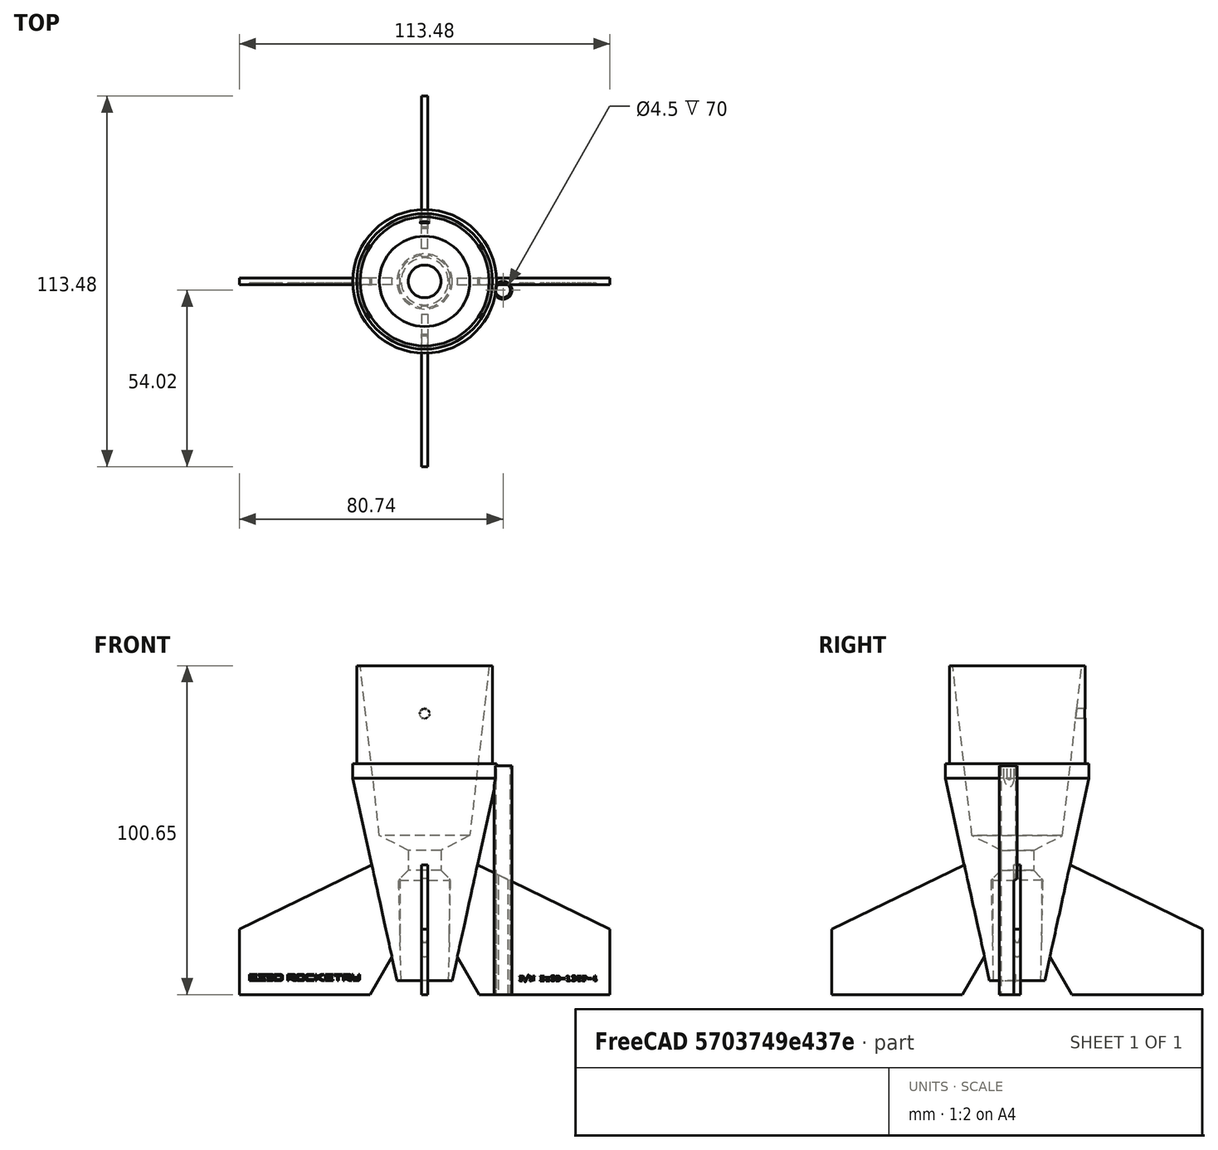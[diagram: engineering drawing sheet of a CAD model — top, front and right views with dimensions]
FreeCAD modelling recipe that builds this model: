
FCSTD DOCUMENT  (FreeCAD 0.20R29603 (Git))
Label: Ez3D-13TP-4
License: All rights reserved
LicenseURL: http://en.wikipedia.org/wiki/All_rights_reserved
objects: Sketcher::SketchObject×4, PartDesign::Pad×2, Part::Part2DObjectPython×2, PartDesign::Pocket×2, PartDesign::Revolution×1, PartDesign::PolarPattern×1, Mesh::Feature×1, PartDesign::Plane×1, PartDesign::Hole×1, PartDesign::Body×1
note: 21 computed .brp shape members not serialized (recipe doc carries the construction recipe); baked Part::Feature solids carry a one-line shape summary decoded from their .brp

FEATURE [Sketcher::SketchObject] Sketch  label="Fin Can and Transition"
  FullyConstrained = false
  MapMode = 5
  Placement = pos=(0,0,0) rot=(1,0,0;1.5708rad)
  Support = -> [XZ_Plane]
  sketch-geometry (11):
    g0: LineSegment StartX=5 StartY=44.1548 StartZ=0 EndX=5 EndY=38 EndZ=0
    g1: LineSegment StartX=5 StartY=38 StartZ=0 EndX=8 EndY=35 EndZ=0
    g2: LineSegment StartX=8 StartY=35 StartZ=0 EndX=7.21115 EndY=4.32256 EndZ=0
    g3: LineSegment StartX=8.47333 StartY=4.32256 StartZ=0 EndX=22 EndY=66.1942 EndZ=0
    g4: LineSegment StartX=19.75 StartY=100.646 StartZ=0 EndX=13.84 EndY=48.6709 EndZ=0
    g5: LineSegment StartX=13.84 StartY=48.6709 StartZ=0 EndX=5 EndY=44.1548 EndZ=0
    g6: LineSegment StartX=20.75 StartY=70.646 StartZ=0 EndX=20.75 EndY=100.646 EndZ=0
    g7: LineSegment StartX=20.75 StartY=100.646 StartZ=0 EndX=19.75 EndY=100.646 EndZ=0
    g8: LineSegment StartX=20.75 StartY=70.646 StartZ=0 EndX=22 EndY=70.646 EndZ=0
    g9: LineSegment StartX=22 StartY=66.1942 StartZ=0 EndX=22 EndY=70.646 EndZ=0
    g10: LineSegment StartX=8.47333 StartY=4.32256 StartZ=0 EndX=7.21115 EndY=4.32256 EndZ=0
  constraints (25):
    c: Vertical(g0)
    c: Coincident(g0,g1)
    c: Coincident(g1,g2)
    c: Angle(g1) = -0.785398
    c: DistanceX(g-1,g0) = 5
    c: Coincident(g4,g5)
    c: Coincident(g0,g5)
    c: Coincident(g6,g7)
    c: Coincident(g7,g4)
    c: Horizontal(g7)
    c: DistanceX(g-1,g6) = 20.75
    c: DistanceX(g7,g7) = 1
    c: DistanceX(g-1,g3) = 22
    c: Horizontal(g8)
    c: Coincident(g6,g8)
    c: DistanceY(g6,g6) = 30
    c: DistanceX(g-1,g1) = 8
    c: Vertical(g6)
    c: Coincident(g9,g3)
    c: Coincident(g9,g8)
    c: Vertical(g9)
    c: Coincident(g10,g3)
    c: Horizontal(g10)
    c: Coincident(g2,g10)
    c: DistanceY(g-1,g6) = 70.646
FEATURE [PartDesign::Revolution] Revolution  label="Revolution for Fin Can"
  Angle = 360
  Axis = (0,-2e-16,1)
  Base = (0,0,0)
  Placement = pos=(0,0,0) rot=(1,0,0;1.5708rad)
  Profile = -> Sketch
  ReferenceAxis = -> Sketch [V_Axis]
  Reversed = true
FEATURE [Sketcher::SketchObject] Sketch001  label="Fin"
  FullyConstrained = true
  MapMode = 5
  Placement = pos=(0,0,0) rot=(1,0,0;1.5708rad)
  Support = -> [XZ_Plane]
  sketch-geometry (5):
    g0: LineSegment StartX=16.7376 StartY=0 StartZ=0 EndX=56.7376 EndY=0 EndZ=0
    g1: LineSegment StartX=56.7376 StartY=0 StartZ=0 EndX=56.7376 EndY=20 EndZ=0
    g2: LineSegment StartX=56.7376 StartY=20 StartZ=0 EndX=7.5 EndY=44 EndZ=0
    g3: LineSegment StartX=7.5 StartY=44 StartZ=0 EndX=7.5 EndY=16 EndZ=0
    g4: LineSegment StartX=7.5 StartY=16 StartZ=0 EndX=16.7376 EndY=0 EndZ=0
  constraints (15):
    c: Horizontal(g0)
    c: Coincident(g0,g1)
    c: Coincident(g1,g2)
    c: Vertical(g1)
    c: Coincident(g2,g3)
    c: Vertical(g3)
    c: Coincident(g3,g4)
    c: Coincident(g0,g4)
    c: DistanceX(g-1,g2) = 7.5
    c: Angle(g4) = -1.0472
    c: PointOnObject(g0,g-1)
    c: DistanceY(g1,g1) = 20
    c: DistanceX(g0,g0) = 40
    c: DistanceY(g3,g3) = 28
    c: DistanceY(g0,g2) = 44
FEATURE [PartDesign::Pad] Pad  label="Fin 2mm thick"
  BaseFeature = -> Revolution
  Direction = (0,-1,-2e-16)
  Length = 2
  Length2 = 100
  Midplane = true
  Placement = pos=(0,0,0) rot=(1,0,0;1.5708rad)
  Profile = -> Sketch001
  Type = 0
FEATURE [PartDesign::PolarPattern] PolarPattern  label="Add Multiple Fins"
  Angle = 360
  Axis = -> Z_Axis
  BaseFeature = -> Pad
  Occurrences = 4
  Originals = -> [Pad]
  Placement = pos=(0,0,0) rot=(1,0,0;1.5708rad)
FEATURE [Sketcher::SketchObject] Sketch002  label="Launch Lug 4.5mm ID 5.5mm OD"
  FullyConstrained = false
  MapMode = 5
  Support = -> [XY_Plane]
  sketch-geometry (2):
    g0: Circle CenterX=24 CenterY=-2.71977 CenterZ=0 NormalX=0 NormalY=0 NormalZ=1 AngleXU=0 Radius=2.75
    g1: Circle CenterX=24 CenterY=-2.71977 CenterZ=0 NormalX=0 NormalY=0 NormalZ=1 AngleXU=0 Radius=2.25
  constraints (4):
    c: Coincident(g1,g0)
    c: Diameter(g0) = 5.5
    c: Diameter(g1) = 4.5
    c: DistanceX(g-1,g0) = 24
FEATURE [PartDesign::Pad] Pad001  label="Launch Lug 70mm long"
  BaseFeature = -> PolarPattern
  Direction = (0,0,1)
  Length = 70
  Length2 = 100
  Placement = pos=(0,0,0) rot=(1,0,0;1.5708rad)
  Profile = -> Sketch002
  ReferenceAxis = -> Sketch002 [N_Axis]
  Type = 0
FEATURE [Mesh::Feature] _3mmThread20x2_5_5mmTall  label="13mmThread20x2.5-5mmTall"
FEATURE [PartDesign::Plane] DatumPlane  label="DatumPlane for Recovery Harness Hole"
  Length = 137.356
  MapMode = 5
  Placement = pos=(0,-1,1.4e-15) rot=(1,0,0;1.5708rad)
  ResizeMode = 0
  Support = -> [Pad001]
  Width = 149.527
FEATURE [Sketcher::SketchObject] Sketch003  label="Recovery Hanress Hole"
  AttachmentOffset = pos=(0,0,-22) rot=(0,0,1;0rad)
  FullyConstrained = false
  MapMode = 5
  Placement = pos=(0,21,-2.91e-14) rot=(1,0,0;1.5708rad)
  Support = -> [DatumPlane]
  sketch-geometry (1):
    g0: Circle CenterX=0 CenterY=86.0236 CenterZ=0 NormalX=0 NormalY=0 NormalZ=1 AngleXU=0 Radius=1.96722
  constraints (1):
    c: PointOnObject(g0,g-2)
FEATURE [Part::Part2DObjectPython] ShapeString001  label="PN"  # Draft 2D object (typed FeaturePython)
  FontFile = <path>
  MakeFace = true
  Placement = pos=(28.886,-1,4.167) rot=(1,0,0;1.5708rad)
  Size = 2
  String = P/N Ez3D-13TP-4
  Tracking = 0
FEATURE [Part::Part2DObjectPython] ShapeString  label="Logo"  # Draft 2D object (typed FeaturePython)
  FontFile = <path>
  MakeFace = true
  Placement = pos=(-53.849,-1,4.225) rot=(1,0,0;1.5708rad)
  Size = 1.1
  String = Ez3D Rocketry
  Tracking = 0
FEATURE [PartDesign::Pocket] Pocket
  BaseFeature = -> Pad001
  Direction = (0,1,-2e-16)
  Length = 0.5
  Length2 = 5
  Placement = pos=(0,0,0) rot=(1,0,0;1.5708rad)
  Profile = -> ShapeString001
  ReferenceAxis = -> ShapeString001 [N_Axis]
  Type = 0
FEATURE [PartDesign::Pocket] Pocket001
  BaseFeature = -> Pocket
  Direction = (0,1,0)
  Length = 0.5
  Length2 = 5
  Placement = pos=(0,0,0) rot=(1,0,0;1.5708rad)
  Profile = -> ShapeString
  ReferenceAxis = -> ShapeString [N_Axis]
  Type = 0
FEATURE [PartDesign::Hole] Hole  label="Recovery Harness Hole"
  BaseFeature = -> Pocket001
  CustomThreadClearance = 0
  Depth = 35
  DepthType = 0
  Diameter = 3
  DrillForDepth = false
  DrillPoint = 1
  DrillPointAngle = 118
  HoleCutCountersinkAngle = 90
  HoleCutCustomValues = false
  HoleCutDepth = 0
  HoleCutDiameter = 6.1
  HoleCutType = 0
  ModelThread = false
  Placement = pos=(0,0,0) rot=(1,0,0;1.5708rad)
  Profile = -> Sketch003
  Reversed = true
  Tapered = false
  TaperedAngle = 90
  ThreadClass = 0
  ThreadDepth = 35
  ThreadDepthType = 0
  ThreadDirection = 0
  ThreadFit = 0
  ThreadSize = 0
  ThreadType = 0
  Threaded = false
  UseCustomThreadClearance = false
FEATURE [PartDesign::Body] Body
  Group = -> [Sketch,Revolution,Sketch001,Pad,PolarPattern,Sketch002,Pad001,DatumPlane,Sketch003,ShapeString001,ShapeString,Pocket,Pocket001,Hole]
  Origin = -> Origin
  Tip = -> Hole
note: 2 file-system paths scrubbed to <path> (originals preserved in the JSON sidecar)
